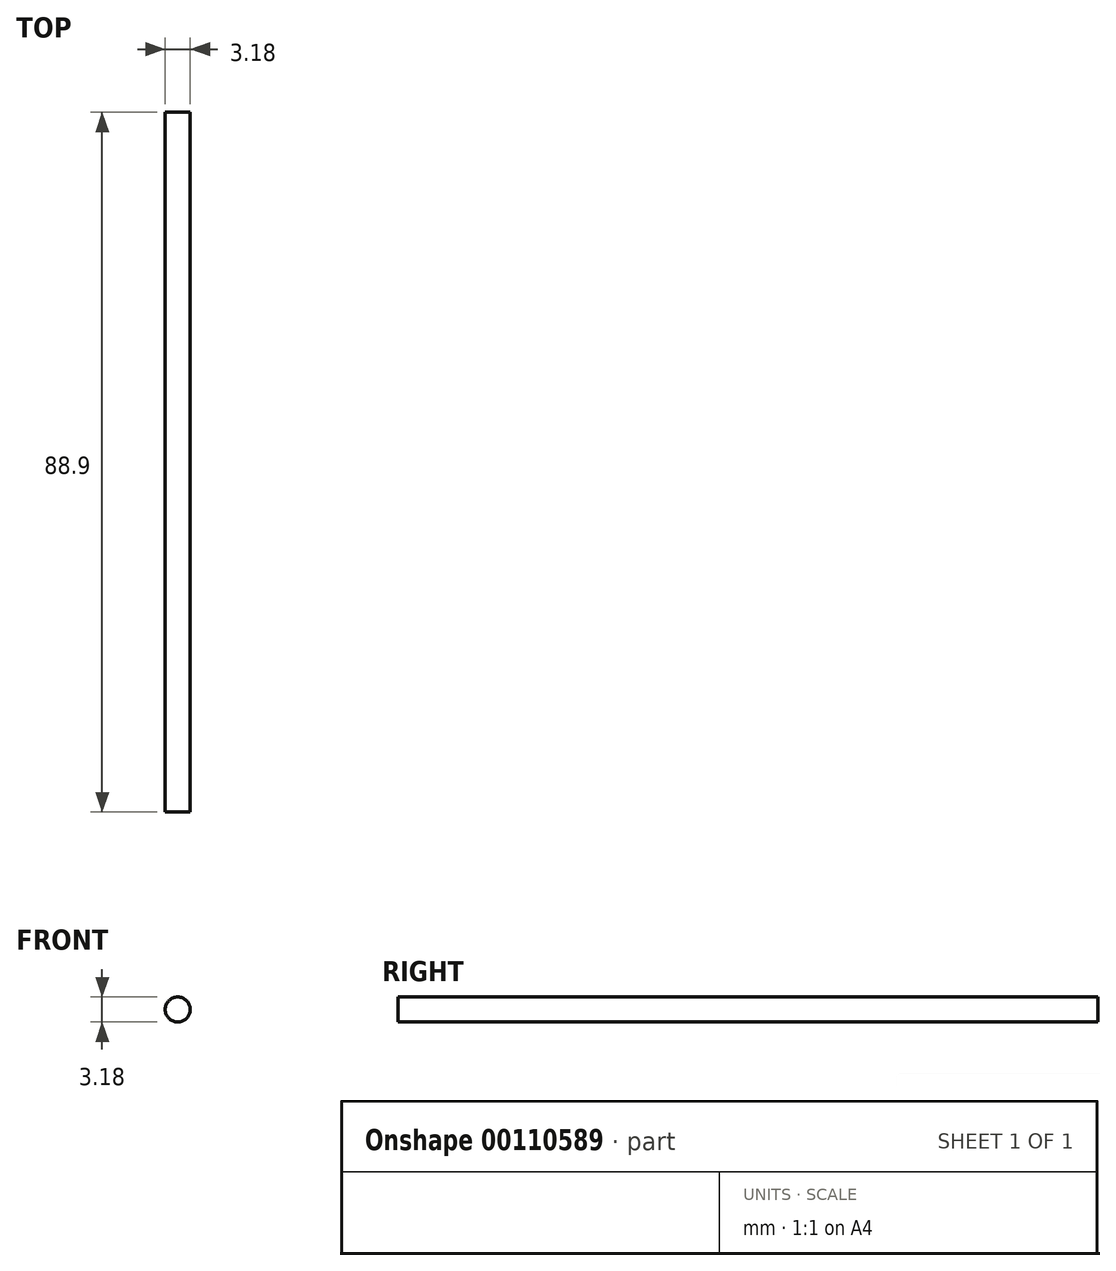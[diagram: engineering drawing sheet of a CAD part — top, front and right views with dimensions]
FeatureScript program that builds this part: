
annotation { "Feature Type Name" : "Feature", "Feature Type Description" : "" }
export const myFeature = defineFeature(function(context is Context, id is Id, definition is map)
    precondition{}
    {
        {
            var Q0;
            Q0=qCreatedBy(makeId("Front.planeOp"),FACE);
            var sketch = newSketch(context, id + "F0", { "sketchPlane" : qUnion([Q0])});
            skCircle(sketch, "E0", {"center": v(0, 0) * mm, "radius": 1.59 * mm});
            skSolve(sketch);
        }
        {
            var Q0;
            Q0=qSketchRegion(id+"F0",true);
            extrude(context, id + "F1", {"entities" : qUnion([Q0]), "depth" : 76.2 * mm});
        }
        {
            var Q0;
            Q0=makeQuery(id+"F1.opExtrude","CAP_FACE",FACE,{"disambiguationData":[OSD([sQuery(id+"F0.wireOp",EDGE,"E0")])],"isStart":false});
            extrude(context, id + "F2", {"entities" : qUnion([Q0]), "operationType" : NewBodyOperationType.ADD, "depth" : 12.7 * mm});
        }
    });
